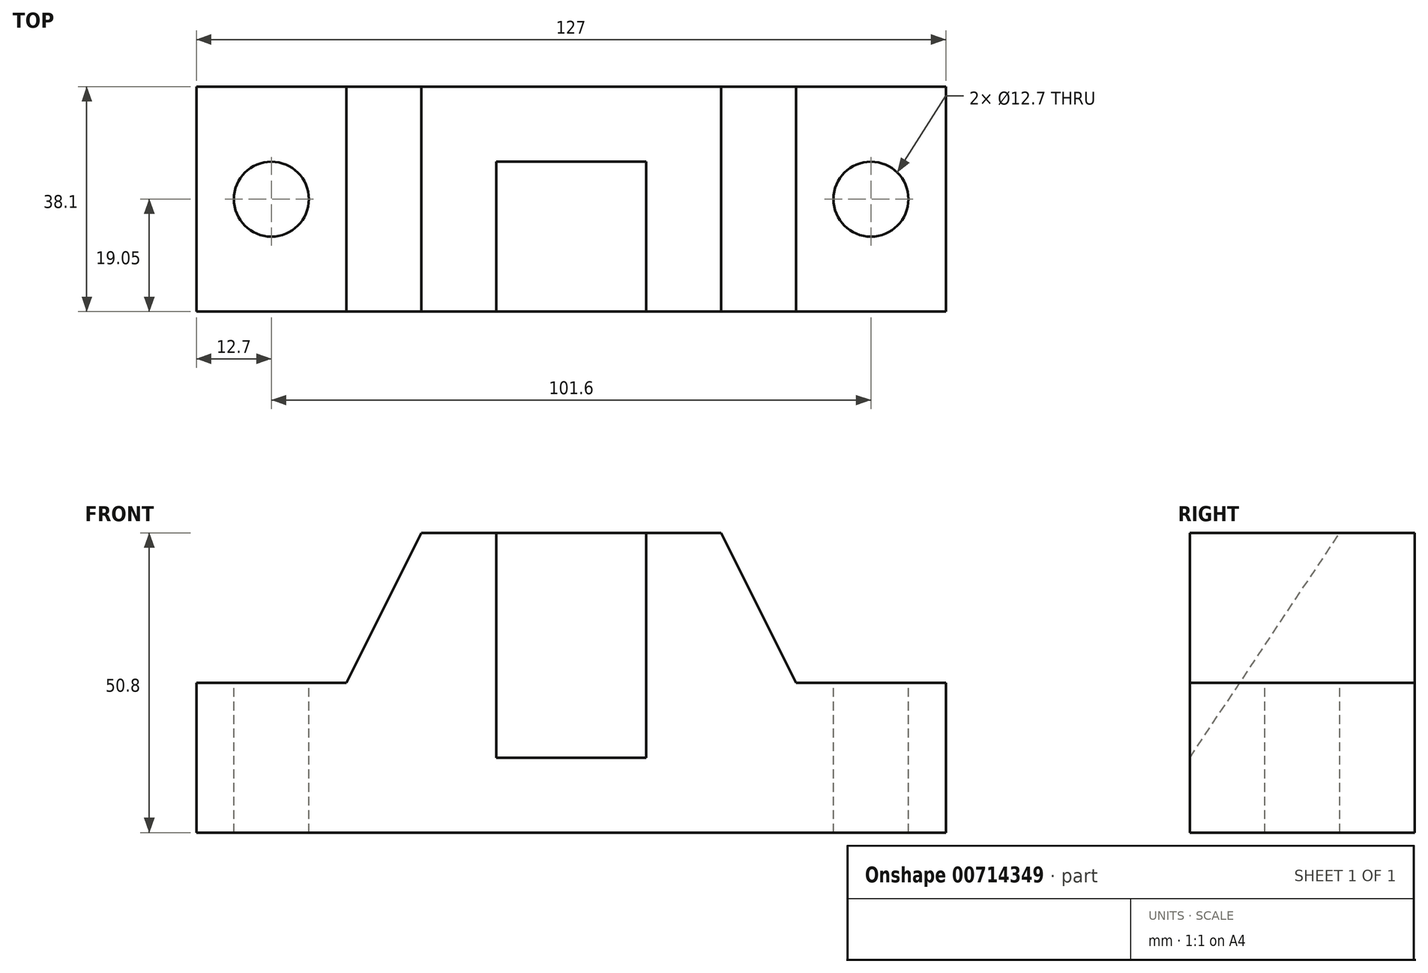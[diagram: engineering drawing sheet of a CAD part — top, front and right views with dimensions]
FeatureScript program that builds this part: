
annotation { "Feature Type Name" : "Feature", "Feature Type Description" : "" }
export const myFeature = defineFeature(function(context is Context, id is Id, definition is map)
    precondition{}
    {
        {
            var Q0;
            Q0=qCreatedBy(makeId("Front.planeOp"),FACE);
            var sketch = newSketch(context, id + "F0", { "sketchPlane" : qUnion([Q0])});
            skLineSegment(sketch, "E0.bottom", {"start": v(-49.47, 24.07) * mm, "end": v(77.53, 24.07) * mm});
            skLineSegment(sketch, "E0.top", {"start": v(-49.47, -26.73) * mm, "end": v(77.53, -26.73) * mm});
            skLineSegment(sketch, "E0.left", {"start": v(-49.47, 24.07) * mm, "end": v(-49.47, -26.73) * mm});
            skLineSegment(sketch, "E0.right", {"start": v(77.53, 24.07) * mm, "end": v(77.53, -26.73) * mm});
            skSolve(sketch);
        }
        {
            var Q0;
            Q0 = qSketchRegion(id + "F0", true);
            extrude(context, id + "F1", {"entities" : qUnion([Q0]), "depth" : 38.1 * mm, "offsetDistance" : 25.4 * mm});
        }
        {
            var Q0;
            Q0=makeQuery(id+"F1.opExtrude","CAP_FACE",FACE,{"disambiguationData":[OSD([sQuery(id+"F0.wireOp",EDGE,"E0.bottom"),sQuery(id+"F0.wireOp",EDGE,"E0.top"),sQuery(id+"F0.wireOp",EDGE,"E0.left"),sQuery(id+"F0.wireOp",EDGE,"E0.right")])],"isStart":false});
            var sketch = newSketch(context, id + "F2", { "sketchPlane" : qUnion([Q0])});
            skLineSegment(sketch, "E1.bottom", {"start": v(-49.47, 24.07) * mm, "end": v(-24.07, 24.07) * mm});
            skLineSegment(sketch, "E1.top", {"start": v(-49.47, -1.33) * mm, "end": v(-24.07, -1.33) * mm});
            skLineSegment(sketch, "E1.left", {"start": v(-49.47, 24.07) * mm, "end": v(-49.47, -1.33) * mm});
            skLineSegment(sketch, "E1.right", {"start": v(-24.07, 24.07) * mm, "end": v(-24.07, -1.33) * mm});
            skLineSegment(sketch, "E2.bottom", {"start": v(77.53, 24.07) * mm, "end": v(52.13, 24.07) * mm});
            skLineSegment(sketch, "E2.top", {"start": v(77.53, -1.33) * mm, "end": v(52.13, -1.33) * mm});
            skLineSegment(sketch, "E2.left", {"start": v(77.53, 24.07) * mm, "end": v(77.53, -1.33) * mm});
            skLineSegment(sketch, "E2.right", {"start": v(52.13, 24.07) * mm, "end": v(52.13, -1.33) * mm});
            skSolve(sketch);
        }
        {
            var Q0;
            Q0=makeQuery(id+"F2.imprint","IMPRINT",FACE,{"disambiguationData":[TD([[makeQuery(id+"F2.imprint","IMPRINT",EDGE,{"derivedFrom":sQuery(id+"F2.wireOp",EDGE,"E1.bottom")}),-1.0]])]});
            var Q1;
            Q1=makeQuery(id+"F2.imprint","IMPRINT",FACE,{"disambiguationData":[TD([[makeQuery(id+"F2.imprint","IMPRINT",EDGE,{"derivedFrom":sQuery(id+"F2.wireOp",EDGE,"E2.bottom")}),-1.0]])]});
            extrude(context, id + "F3", {"entities" : qUnion([Q0, Q1]), "operationType" : NewBodyOperationType.REMOVE, "endBound" : BoundingType.THROUGH_ALL, "oppositeDirection" : true, "depth" : 25.4 * mm, "offsetDistance" : 25.4 * mm});
        }
        {
            var Q0;
            Q0=makeQuery(id+"F1.opExtrude","CAP_FACE",FACE,{"disambiguationData":[OSD([sQuery(id+"F0.wireOp",EDGE,"E0.bottom"),sQuery(id+"F0.wireOp",EDGE,"E0.top"),sQuery(id+"F0.wireOp",EDGE,"E0.left"),sQuery(id+"F0.wireOp",EDGE,"E0.right")])],"isStart":false});
            var sketch = newSketch(context, id + "F4", { "sketchPlane" : qUnion([Q0])});
            skLineSegment(sketch, "E3", {"start": v(-24.07, -1.33) * mm, "end": v(-11.37, 24.07) * mm});
            skLineSegment(sketch, "E4", {"start": v(-11.37, 24.07) * mm, "end": v(39.43, 24.07) * mm});
            skLineSegment(sketch, "E5", {"start": v(39.43, 24.07) * mm, "end": v(52.13, -1.33) * mm});
            skSolve(sketch);
        }
        {
            var Q0;
            {var subQ0=sQuery(id+"F4.wireOp",EDGE,"E3");Q0=makeQuery(id+"F4.imprint","IMPRINT",FACE,{"disambiguationData":[TD([[makeQuery(id+"F4.imprint","IMPRINT",EDGE,{"derivedFrom":subQ0}),1.0]])]});}
            var Q1;
            {var subQ0=sQuery(id+"F4.wireOp",EDGE,"E5");Q1=makeQuery(id+"F4.imprint","IMPRINT",FACE,{"disambiguationData":[TD([[makeQuery(id+"F4.imprint","IMPRINT",EDGE,{"derivedFrom":subQ0}),1.0]])]});}
            extrude(context, id + "F5", {"entities" : qUnion([Q0, Q1]), "operationType" : NewBodyOperationType.REMOVE, "endBound" : BoundingType.THROUGH_ALL, "oppositeDirection" : true, "depth" : 25.4 * mm, "offsetDistance" : 25.4 * mm});
        }
        {
            var Q0;
            Q0=makeQuery(id+"F1.opExtrude","CAP_FACE",FACE,{"disambiguationData":[OSD([sQuery(id+"F0.wireOp",EDGE,"E0.bottom"),sQuery(id+"F0.wireOp",EDGE,"E0.top"),sQuery(id+"F0.wireOp",EDGE,"E0.left"),sQuery(id+"F0.wireOp",EDGE,"E0.right")])],"isStart":false});
            var sketch = newSketch(context, id + "F6", { "sketchPlane" : qUnion([Q0])});
            skLineSegment(sketch, "E6.bottom", {"start": v(1.33, 24.07) * mm, "end": v(26.73, 24.07) * mm});
            skLineSegment(sketch, "E6.top", {"start": v(1.33, -14.03) * mm, "end": v(26.73, -14.03) * mm});
            skLineSegment(sketch, "E6.left", {"start": v(1.33, 24.07) * mm, "end": v(1.33, -14.03) * mm});
            skLineSegment(sketch, "E6.right", {"start": v(26.73, 24.07) * mm, "end": v(26.73, -14.03) * mm});
            skSolve(sketch);
        }
        {
            var Q0;
            Q0=makeQuery(id+"F3.boolean.opBoolean","COPY",FACE,{"derivedFrom":makeQuery(id+"F3.opExtrude","SWEPT_FACE",FACE,{"disambiguationData":[OSD([sQuery(id+"F2.wireOp",EDGE,"E1.top")])]})});
            var sketch = newSketch(context, id + "F7", { "sketchPlane" : qUnion([Q0])});
            skCircle(sketch, "E7", {"center": v(-36.77, -19.05) * mm, "radius": 6.35 * mm});
            skSolve(sketch);
        }
        {
            var Q0;
            Q0=makeQuery(id+"F3.boolean.opBoolean","COPY",FACE,{"derivedFrom":makeQuery(id+"F3.opExtrude","SWEPT_FACE",FACE,{"disambiguationData":[OSD([sQuery(id+"F2.wireOp",EDGE,"E2.top")])]})});
            var sketch = newSketch(context, id + "F8", { "sketchPlane" : qUnion([Q0])});
            skCircle(sketch, "E8", {"center": v(64.83, -19.05) * mm, "radius": 6.35 * mm});
            skSolve(sketch);
        }
        {
            var Q0;
            Q0=makeQuery(id+"F8.imprint","IMPRINT",FACE,{"disambiguationData":[TD([[makeQuery(id+"F8.imprint","IMPRINT",EDGE,{"derivedFrom":sQuery(id+"F8.wireOp",EDGE,"E8")}),1.0]])]});
            var Q1;
            Q1=makeQuery(id+"F7.imprint","IMPRINT",FACE,{"disambiguationData":[TD([[makeQuery(id+"F7.imprint","IMPRINT",EDGE,{"derivedFrom":sQuery(id+"F7.wireOp",EDGE,"E7")}),1.0]])]});
            extrude(context, id + "F9", {"entities" : qUnion([Q0, Q1]), "operationType" : NewBodyOperationType.REMOVE, "endBound" : BoundingType.THROUGH_ALL, "oppositeDirection" : true, "depth" : 25.4 * mm, "offsetDistance" : 25.4 * mm});
        }
        {
            var Q0;
            Q0=makeQuery(id+"F6.imprint","IMPRINT",FACE,{"disambiguationData":[TD([[makeQuery(id+"F6.imprint","IMPRINT",EDGE,{"derivedFrom":sQuery(id+"F6.wireOp",EDGE,"E6.bottom")}),-1.0]])]});
            extrude(context, id + "F10", {"entities" : qUnion([Q0]), "operationType" : NewBodyOperationType.REMOVE, "oppositeDirection" : true, "depth" : 25.4 * mm, "offsetDistance" : 25.4 * mm});
        }
        {
            var Q0;
            Q0=makeQuery(id+"F10.boolean.opBoolean","COPY",FACE,{"derivedFrom":makeQuery(id+"F10.opExtrude","SWEPT_FACE",FACE,{"disambiguationData":[OSD([sQuery(id+"F6.wireOp",EDGE,"E6.left")])]})});
            var sketch = newSketch(context, id + "F11", { "sketchPlane" : qUnion([Q0])});
            skLineSegment(sketch, "E9", {"start": v(-38.1, -14.03) * mm, "end": v(-12.7, 24.07) * mm});
            skSolve(sketch);
        }
        {
            var Q0;
            Q0=makeQuery(id+"F11.imprint","IMPRINT",FACE,{"disambiguationData":[TD([[makeQuery(id+"F11.imprint","IMPRINT",EDGE,{"derivedFrom":sQuery(id+"F11.wireOp",EDGE,"E9")}),-1.0]])]});
            extrude(context, id + "F12", {"entities" : qUnion([Q0]), "operationType" : NewBodyOperationType.ADD, "depth" : 25.4 * mm, "offsetDistance" : 25.4 * mm});
        }
    });
